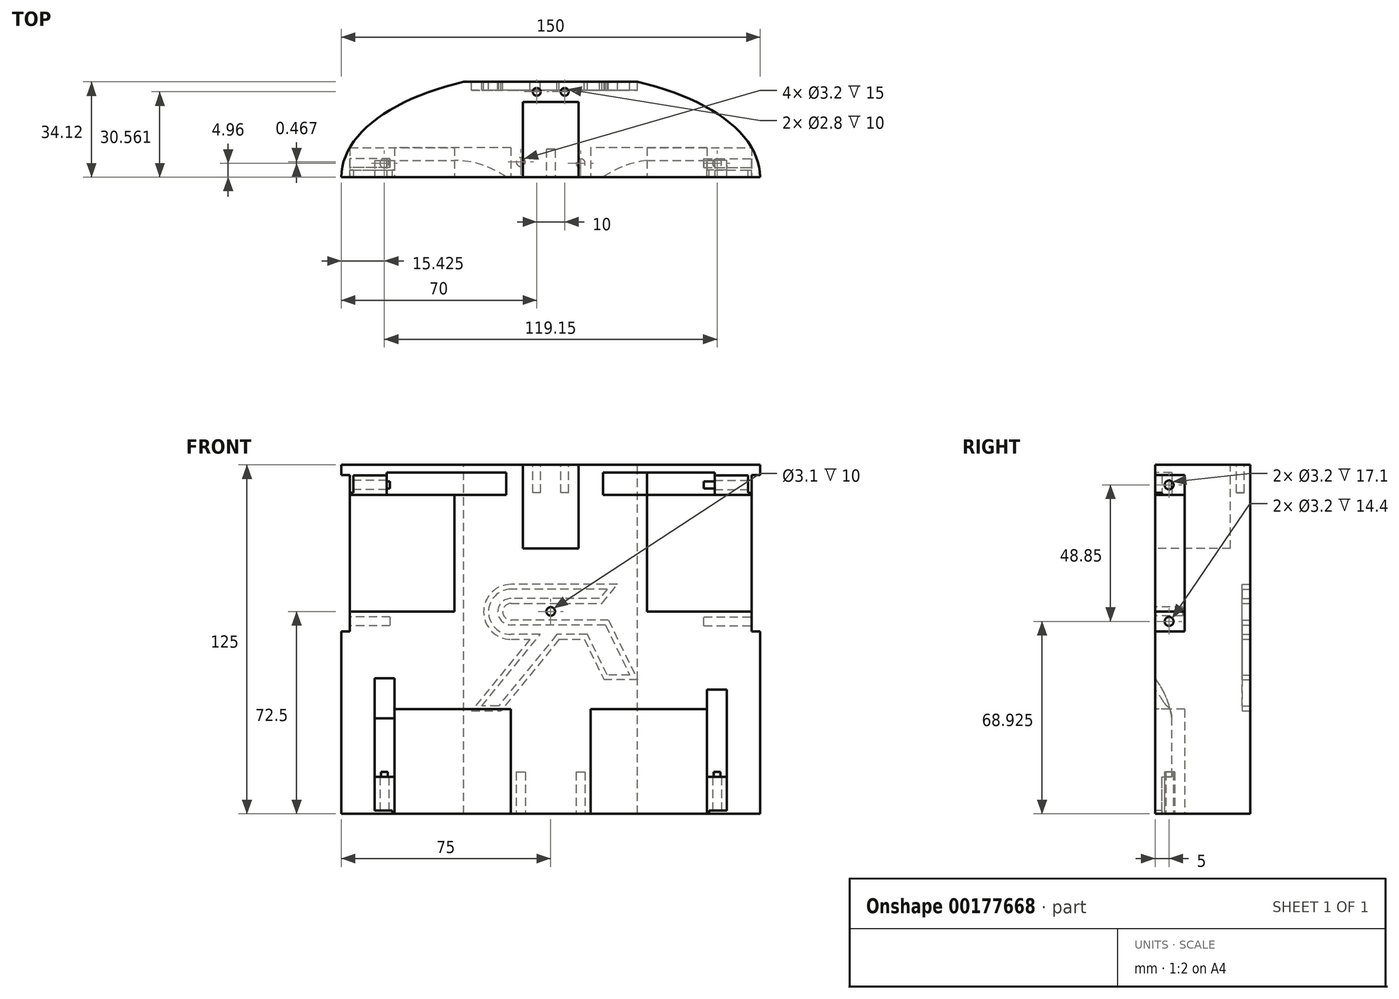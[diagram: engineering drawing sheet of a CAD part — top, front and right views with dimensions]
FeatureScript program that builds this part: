
annotation { "Feature Type Name" : "Feature", "Feature Type Description" : "" }
export const myFeature = defineFeature(function(context is Context, id is Id, definition is map)
    precondition{}
    {
        {
            var Q0;
            Q0=qCreatedBy(makeId("Top.planeOp"),FACE);
            var sketch = newSketch(context, id + "F0", { "sketchPlane" : qUnion([Q0])});
            skLineSegment(sketch, "E0.bottom", {"start": v(-150, 0) * mm, "end": v(0, 0) * mm});
            skLineSegment(sketch, "E0.top", {"start": v(-150, -75) * mm, "end": v(0, -75) * mm});
            skLineSegment(sketch, "E0.left", {"start": v(-150, 0) * mm, "end": v(-150, -75) * mm});
            skLineSegment(sketch, "E0.right", {"start": v(0, 0) * mm, "end": v(0, -75) * mm});
            skLineSegment(sketch, "E1", {"start": v(0, -37.5) * mm, "end": v(-150, -37.5) * mm});
            skPoint(sketch, "E2", {"position": v(-75, -37.5) * mm});
            skEllipse(sketch, "E3", {"center": v(-75, -37.5) * mm, "majorRadius": 75 * mm, "minorRadius": 37.5 * mm, "majorAxis": v(1, 0)});
            skSolve(sketch);
        }
        {
            var Q0;
            {var subQ0=sQuery(id+"F0.wireOp",EDGE,"E1");Q0=makeQuery(id+"F0.imprint","IMPRINT",FACE,{"disambiguationData":[TD([[makeQuery(id+"F0.imprint","IMPRINT",EDGE,{"derivedFrom":subQ0}),1.0]])]});}
            var Q1;
            {var subQ0=sQuery(id+"F0.wireOp",EDGE,"E1");Q1=makeQuery(id+"F0.imprint","IMPRINT",FACE,{"disambiguationData":[TD([[makeQuery(id+"F0.imprint","IMPRINT",EDGE,{"derivedFrom":subQ0}),-1.0]])]});}
            extrude(context, id + "F1", {"entities" : qUnion([Q0, Q1]), "depth" : 125 * mm});
        }
        {
            var Q0;
            Q0=qCreatedBy(makeId("Right.planeOp"),FACE);
            var sketch = newSketch(context, id + "F2", { "sketchPlane" : qUnion([Q0])});
            skLineSegment(sketch, "E4.bottom", {"start": v(-48.1, 114.2) * mm, "end": v(-26.9, 114.2) * mm});
            skLineSegment(sketch, "E4.top", {"start": v(-48.1, 72.5) * mm, "end": v(-26.9, 72.5) * mm});
            skLineSegment(sketch, "E4.left", {"start": v(-48.1, 114.2) * mm, "end": v(-48.1, 72.5) * mm});
            skLineSegment(sketch, "E4.right", {"start": v(-26.9, 114.2) * mm, "end": v(-26.9, 72.5) * mm});
            skPoint(sketch, "E5", {"position": v(-37.5, 125) * mm});
            skPoint(sketch, "E6", {"position": v(-37.5, 114.2) * mm});
            skLineSegment(sketch, "E7", {"start": v(-37.5, 125) * mm, "end": v(-37.5, 121.35) * mm});
            skLineSegment(sketch, "E8.bottom", {"start": v(-48.1, 113.35) * mm, "end": v(-26.9, 113.35) * mm, "construction": true});
            skLineSegment(sketch, "E8.top", {"start": v(-48.1, 73.35) * mm, "end": v(-26.9, 73.35) * mm, "construction": true});
            skLineSegment(sketch, "E8.left", {"start": v(-48.1, 113.35) * mm, "end": v(-48.1, 73.35) * mm, "construction": true});
            skLineSegment(sketch, "E8.right", {"start": v(-26.9, 113.35) * mm, "end": v(-26.9, 73.35) * mm, "construction": true});
            skPoint(sketch, "E9", {"position": v(-26.9, 93.35) * mm});
            skLineSegment(sketch, "E10.bottom", {"start": v(-48.1, 113.35) * mm, "end": v(-26.9, 113.35) * mm});
            skLineSegment(sketch, "E10.top", {"start": v(-48.1, 121.35) * mm, "end": v(-26.9, 121.35) * mm});
            skLineSegment(sketch, "E10.left", {"start": v(-48.1, 113.35) * mm, "end": v(-48.1, 121.35) * mm});
            skLineSegment(sketch, "E10.right", {"start": v(-26.9, 113.35) * mm, "end": v(-26.9, 121.35) * mm});
            skLineSegment(sketch, "E11.bottom", {"start": v(-48.1, 73.35) * mm, "end": v(-26.9, 73.35) * mm});
            skLineSegment(sketch, "E11.top", {"start": v(-48.1, 65.35) * mm, "end": v(-26.9, 65.35) * mm});
            skLineSegment(sketch, "E11.left", {"start": v(-48.1, 73.35) * mm, "end": v(-48.1, 65.35) * mm});
            skLineSegment(sketch, "E11.right", {"start": v(-26.9, 73.35) * mm, "end": v(-26.9, 65.35) * mm});
            skLineSegment(sketch, "E12", {"start": v(-37.5, 65.35) * mm, "end": v(-37.5, 0) * mm});
            skLineSegment(sketch, "E13", {"start": v(-37.5, 121.35) * mm, "end": v(-37.5, 125) * mm});
            skLineSegment(sketch, "E14.trimOffspring", {"start": v(-37.5, 114.2) * mm, "end": v(-37.5, 72.5) * mm});
            skSolve(sketch);
        }
        {
            var Q0;
            {var subQ0=sQuery(id+"F2.wireOp",EDGE,"E4.right");Q0=makeQuery(id+"F2.imprint","IMPRINT",FACE,{"disambiguationData":[TD([[makeQuery(id+"F2.imprint","IMPRINT",EDGE,{"derivedFrom":subQ0}),-1.0]])]});}
            var Q1;
            {var subQ0=sQuery(id+"F2.wireOp",EDGE,"E4.left");Q1=makeQuery(id+"F2.imprint","IMPRINT",FACE,{"disambiguationData":[TD([[makeQuery(id+"F2.imprint","IMPRINT",EDGE,{"derivedFrom":subQ0}),1.0]])]});}
            var Q2;
            {var subQ0=sQuery(id+"F2.wireOp",EDGE,"E11.left");var subQ1=sQuery(id+"F2.wireOp",EDGE,"E4.top");var subQ2=makeQuery(id+"F2.imprint","INTERSECT",VERTEX,{"derivedFrom":[subQ1,subQ0]});Q2=makeQuery(id+"F2.imprint","IMPRINT",FACE,{"disambiguationData":[TD([[makeQuery(id+"F2.imprint","IMPRINT",EDGE,{"disambiguationData":[TD([[subQ2,-1.0]])],"derivedFrom":subQ1}),1.0]])]});}
            var Q3;
            {var subQ0=sQuery(id+"F2.wireOp",EDGE,"E11.right");var subQ1=sQuery(id+"F2.wireOp",EDGE,"E4.top");var subQ2=makeQuery(id+"F2.imprint","INTERSECT",VERTEX,{"derivedFrom":[subQ1,subQ0]});Q3=makeQuery(id+"F2.imprint","IMPRINT",FACE,{"disambiguationData":[TD([[makeQuery(id+"F2.imprint","IMPRINT",EDGE,{"disambiguationData":[TD([[subQ2,1.0]])],"derivedFrom":subQ1}),1.0]])]});}
            var Q4;
            {var subQ0=sQuery(id+"F2.wireOp",EDGE,"E10.left");var subQ1=sQuery(id+"F2.wireOp",EDGE,"E4.bottom");var subQ2=makeQuery(id+"F2.imprint","INTERSECT",VERTEX,{"derivedFrom":[subQ1,subQ0]});Q4=makeQuery(id+"F2.imprint","IMPRINT",FACE,{"disambiguationData":[TD([[makeQuery(id+"F2.imprint","IMPRINT",EDGE,{"disambiguationData":[TD([[subQ2,-1.0]])],"derivedFrom":subQ1}),-1.0]])]});}
            var Q5;
            {var subQ0=sQuery(id+"F2.wireOp",EDGE,"E10.right");var subQ1=sQuery(id+"F2.wireOp",EDGE,"E4.bottom");var subQ2=makeQuery(id+"F2.imprint","INTERSECT",VERTEX,{"derivedFrom":[subQ1,subQ0]});Q5=makeQuery(id+"F2.imprint","IMPRINT",FACE,{"disambiguationData":[TD([[makeQuery(id+"F2.imprint","IMPRINT",EDGE,{"disambiguationData":[TD([[subQ2,1.0]])],"derivedFrom":subQ1}),-1.0]])]});}
            extrude(context, id + "F3", {"entities" : qUnion([Q0, Q1, Q2, Q3, Q4, Q5]), "operationType" : NewBodyOperationType.REMOVE, "oppositeDirection" : true, "depth" : 155.5 * mm});
        }
        {
            var Q0;
            Q0=makeQuery(id+"F3.boolean.opBoolean","COPY",FACE,{"derivedFrom":makeQuery(id+"F3.opExtrude","SWEPT_FACE",FACE,{"disambiguationData":[OSD([sQuery(id+"F2.wireOp",EDGE,"E4.top")])]})});
            var sketch = newSketch(context, id + "F4", { "sketchPlane" : qUnion([Q0])});
            skLineSegment(sketch, "E15", {"start": v(-3.06, -48.1) * mm, "end": v(-3.06, -26.9) * mm});
            skEllipticalArc(sketch, "E16.0", {});
            skLineSegment(sketch, "E17", {"start": v(-146.94, -48.1) * mm, "end": v(-146.94, -26.9) * mm});
            skEllipticalArc(sketch, "E18.0", {});
            const initialGuessF4  = {"E16.0": [-0.075, -0.0375, 1, 0, 0.075, 0.0375, 5.996612290444908, 0.28657301673467844], "E18.0": [-0.075, -0.0375, 1, 0, 0.075, 0.0375, 2.855019636855115, 3.428165670324471]};
            skSetInitialGuess(sketch, initialGuessF4);
            skSolve(sketch);
        }
        {
            var Q0;
            Q0=makeQuery(id+"F4.imprint","IMPRINT",FACE,{"disambiguationData":[TD([[makeQuery(id+"F4.imprint","IMPRINT",EDGE,{"derivedFrom":sQuery(id+"F4.wireOp",EDGE,"E17")}),1.0]])]});
            var Q1;
            Q1=makeQuery(id+"F4.imprint","IMPRINT",FACE,{"disambiguationData":[TD([[makeQuery(id+"F4.imprint","IMPRINT",EDGE,{"derivedFrom":sQuery(id+"F4.wireOp",EDGE,"E15")}),-1.0]])]});
            extrude(context, id + "F5", {"entities" : qUnion([Q0, Q1]), "operationType" : NewBodyOperationType.REMOVE, "oppositeDirection" : true, "depth" : 7.15 * mm});
        }
        {
            var Q0;
            Q0=makeQuery(id+"F3.boolean.opBoolean","COPY",FACE,{"derivedFrom":makeQuery(id+"F3.opExtrude","SWEPT_FACE",FACE,{"disambiguationData":[OSD([sQuery(id+"F2.wireOp",EDGE,"E4.bottom")])]})});
            var sketch = newSketch(context, id + "F6", { "sketchPlane" : qUnion([Q0])});
            skLineSegment(sketch, "E19", {"start": v(-3.06, 26.9) * mm, "end": v(-3.06, 48.1) * mm});
            skEllipticalArc(sketch, "E20.0", {});
            skLineSegment(sketch, "E21", {"start": v(-146.94, 26.9) * mm, "end": v(-146.94, 48.1) * mm});
            skEllipticalArc(sketch, "E22.0", {});
            const initialGuessF6  = {"E20.0": [-0.075, 0.0375, 1, 0, 0.075, 0.0375, 5.996612290444908, 0.28657301673467805], "E22.0": [-0.075, 0.0375, 1, 0, 0.075, 0.0375, 2.8550196368551153, 3.428165670324471]};
            skSetInitialGuess(sketch, initialGuessF6);
            skSolve(sketch);
        }
        {
            var Q0;
            Q0=makeQuery(id+"F6.imprint","IMPRINT",FACE,{"disambiguationData":[TD([[makeQuery(id+"F6.imprint","IMPRINT",EDGE,{"derivedFrom":sQuery(id+"F6.wireOp",EDGE,"E21")}),1.0]])]});
            var Q1;
            Q1=makeQuery(id+"F6.imprint","IMPRINT",FACE,{"disambiguationData":[TD([[makeQuery(id+"F6.imprint","IMPRINT",EDGE,{"derivedFrom":sQuery(id+"F6.wireOp",EDGE,"E19")}),-1.0]])]});
            extrude(context, id + "F7", {"entities" : qUnion([Q0, Q1]), "operationType" : NewBodyOperationType.REMOVE, "oppositeDirection" : true, "depth" : 7.15 * mm});
        }
        {
            var Q0;
            Q0=makeQuery(id+"F3.boolean.opBoolean","COPY",FACE,{"derivedFrom":makeQuery(id+"F3.opExtrude","SWEPT_FACE",FACE,{"disambiguationData":[OSD([sQuery(id+"F2.wireOp",EDGE,"E4.top")])]})});
            var sketch = newSketch(context, id + "F8", { "sketchPlane" : qUnion([Q0])});
            skLineSegment(sketch, "E23.bottom", {"start": v(-109.44, -26.9) * mm, "end": v(-40.56, -26.9) * mm});
            skLineSegment(sketch, "E23.top", {"start": v(-109.44, -48.1) * mm, "end": v(-40.56, -48.1) * mm});
            skLineSegment(sketch, "E23.left", {"start": v(-109.44, -26.9) * mm, "end": v(-109.44, -48.1) * mm});
            skLineSegment(sketch, "E23.right", {"start": v(-40.56, -26.9) * mm, "end": v(-40.56, -48.1) * mm});
            skSolve(sketch);
        }
        {
            var Q0;
            Q0=makeQuery(id+"F8.imprint","IMPRINT",FACE,{"disambiguationData":[TD([[makeQuery(id+"F8.imprint","IMPRINT",EDGE,{"derivedFrom":sQuery(id+"F8.wireOp",EDGE,"E23.bottom")}),-1.0]])]});
            extrude(context, id + "F9", {"entities" : qUnion([Q0]), "operationType" : NewBodyOperationType.ADD, "depth" : 46 * mm});
        }
        {
            var Q0;
            Q0=makeQuery(id+"F9.boolean.opBoolean","SPLIT",FACE,{"disambiguationData":[TD([makeQuery(id+"F7.boolean.opBoolean","COPY",FACE,{"derivedFrom":makeQuery(id+"F7.opExtrude","SWEPT_FACE",FACE,{"disambiguationData":[OSD([sQuery(id+"F6.wireOp",EDGE,"E21")])]})})])],"derivedFrom":makeQuery(id+"F3.boolean.opBoolean","COPY",FACE,{"derivedFrom":makeQuery(id+"F3.opExtrude","SWEPT_FACE",FACE,{"disambiguationData":[OSD([sQuery(id+"F2.wireOp",EDGE,"E4.bottom")])]})})});
            var sketch = newSketch(context, id + "F10", { "sketchPlane" : qUnion([Q0])});
            skLineSegment(sketch, "E24", {"start": v(-145.7, 26.9) * mm, "end": v(-145.7, 48.1) * mm, "construction": true});
            skLineSegment(sketch, "E25", {"start": v(-145.7, 37.5) * mm, "end": v(-142.91, 37.5) * mm});
            skLineSegment(sketch, "E26.bottom", {"start": v(-145.7, 35) * mm, "end": v(-4.3, 35) * mm});
            skLineSegment(sketch, "E26.top", {"start": v(-145.7, 40) * mm, "end": v(-4.3, 40) * mm});
            skLineSegment(sketch, "E26.left", {"start": v(-145.7, 35) * mm, "end": v(-145.7, 40) * mm});
            skLineSegment(sketch, "E26.right", {"start": v(-4.3, 35) * mm, "end": v(-4.3, 40) * mm});
            skLineSegment(sketch, "E27", {"start": v(-4.3, 26.9) * mm, "end": v(-4.3, 48.1) * mm, "construction": true});
            skLineSegment(sketch, "E28", {"start": v(-145.7, 37.5) * mm, "end": v(-145.7, 40) * mm});
            skLineSegment(sketch, "E29", {"start": v(-145.7, 35) * mm, "end": v(-145.7, 37.5) * mm});
            skSolve(sketch);
        }
        {
            var Q0;
            Q0=qSketchRegion(id+"F10",true);
            extrude(context, id + "F11", {"entities" : qUnion([Q0]), "operationType" : NewBodyOperationType.REMOVE, "oppositeDirection" : true, "depth" : 7 * mm});
        }
        {
            var Q0;
            Q0=makeQuery(id+"F9.boolean.opBoolean","SPLIT",FACE,{"disambiguationData":[TD([makeQuery(id+"F7.boolean.opBoolean","COPY",FACE,{"derivedFrom":makeQuery(id+"F7.opExtrude","SWEPT_FACE",FACE,{"disambiguationData":[OSD([sQuery(id+"F6.wireOp",EDGE,"E21")])]})})])],"derivedFrom":makeQuery(id+"F3.boolean.opBoolean","COPY",FACE,{"derivedFrom":makeQuery(id+"F3.opExtrude","SWEPT_FACE",FACE,{"disambiguationData":[OSD([sQuery(id+"F2.wireOp",EDGE,"E4.bottom")])]})})});
            var sketch = newSketch(context, id + "F12", { "sketchPlane" : qUnion([Q0])});
            skLineSegment(sketch, "E30.bottom", {"start": v(-133.7, 31.5) * mm, "end": v(-16.3, 31.5) * mm});
            skLineSegment(sketch, "E30.top", {"start": v(-133.7, 43.5) * mm, "end": v(-16.3, 43.5) * mm});
            skLineSegment(sketch, "E30.left", {"start": v(-133.7, 31.5) * mm, "end": v(-133.7, 43.5) * mm});
            skLineSegment(sketch, "E30.right", {"start": v(-16.3, 31.5) * mm, "end": v(-16.3, 43.5) * mm});
            skLineSegment(sketch, "E31", {"start": v(-133.7, 35) * mm, "end": v(-133.7, 40) * mm});
            skPoint(sketch, "E32", {"position": v(-133.7, 37.5) * mm});
            skLineSegment(sketch, "E33", {"start": v(-16.3, 35) * mm, "end": v(-16.3, 40) * mm});
            skPoint(sketch, "E34", {"position": v(-16.3, 37.5) * mm});
            skSolve(sketch);
        }
        {
            var Q0;
            Q0=qSketchRegion(id+"F12",true);
            extrude(context, id + "F13", {"entities" : qUnion([Q0]), "operationType" : NewBodyOperationType.REMOVE, "oppositeDirection" : true, "depth" : 8 * mm});
        }
        {
            var Q0;
            Q0=makeQuery(id+"F9.boolean.opBoolean","SPLIT",FACE,{"disambiguationData":[TD([makeQuery(id+"F7.boolean.opBoolean","COPY",FACE,{"derivedFrom":makeQuery(id+"F7.opExtrude","SWEPT_FACE",FACE,{"disambiguationData":[OSD([sQuery(id+"F6.wireOp",EDGE,"E21")])]})})])],"derivedFrom":makeQuery(id+"F3.boolean.opBoolean","COPY",FACE,{"derivedFrom":makeQuery(id+"F3.opExtrude","SWEPT_FACE",FACE,{"disambiguationData":[OSD([sQuery(id+"F2.wireOp",EDGE,"E4.bottom")])]})})});
            var sketch = newSketch(context, id + "F14", { "sketchPlane" : qUnion([Q0])});
            skArc(sketch, "E35", {"start": v(-109.44, 31.5) * mm, "mid": v(-83.34, 45.45) * mm, "end": v(-80.45, 74.9) * mm});
            skArc(sketch, "E36", {"start": v(-109.44, 43.5) * mm, "mid": v(-91.99, 53.74) * mm, "end": v(-92.41, 73.98) * mm});
            skEllipticalArc(sketch, "E37.0", {});
            skLineSegment(sketch, "E38", {"start": v(-109.44, 31.5) * mm, "end": v(-109.44, 43.5) * mm});
            skArc(sketch, "E39", {"start": v(-69.55, 74.9) * mm, "mid": v(-65.03, 46.53) * mm, "end": v(-40.56, 31.5) * mm});
            skArc(sketch, "E40", {"start": v(-57.59, 73.98) * mm, "mid": v(-55.43, 55.19) * mm, "end": v(-40.56, 43.5) * mm});
            skEllipticalArc(sketch, "E41.0", {});
            skLineSegment(sketch, "E42", {"start": v(-40.56, 31.5) * mm, "end": v(-40.56, 43.5) * mm});
            skLineSegment(sketch, "E43", {"start": v(-75, 37.5) * mm, "end": v(-75, 74.9) * mm, "construction": true});
            skLineSegment(sketch, "E44", {"start": v(-69.55, 74.9) * mm, "end": v(-75, 74.9) * mm, "construction": true});
            skLineSegment(sketch, "E45", {"start": v(-80.45, 74.9) * mm, "end": v(-75, 74.9) * mm, "construction": true});
            const initialGuessF14  = {"E37.0": [-0.075, 0.0375, 1, 0, 0.075, 0.0375, 1.6434997456011395, 1.8050969396186902], "E41.0": [-0.075, 0.0375, 1, 0, 0.075, 0.0375, 1.3364957139711027, 1.4980929079886538], "E37.0": [-0.075, 0.0375, 1, 0, 0.075, 0.0375, 1.6434997456011395, 1.8050969396186902]};
            skSetInitialGuess(sketch, initialGuessF14);
            skSolve(sketch);
        }
        {
            var Q0;
            Q0=qSketchRegion(id+"F14",true);
            extrude(context, id + "F15", {"entities" : qUnion([Q0]), "operationType" : NewBodyOperationType.REMOVE, "oppositeDirection" : true, "depth" : 8 * mm});
        }
        {
            var Q0;
            Q0=makeQuery(id+"F15.boolean.opBoolean","MERGE",FACE,{"derivedFrom":[makeQuery(id+"F13.boolean.opBoolean","MERGE",FACE,{"derivedFrom":[makeQuery(id+"F11.boolean.opBoolean","COPY",FACE,{"derivedFrom":makeQuery(id+"F11.opExtrude","CAP_FACE",FACE,{"disambiguationData":[OSD([sQuery(id+"F10.wireOp",EDGE,"E26.bottom"),sQuery(id+"F10.wireOp",EDGE,"E26.top"),sQuery(id+"F10.wireOp",EDGE,"E26.right"),sQuery(id+"F10.wireOp",EDGE,"E28"),sQuery(id+"F10.wireOp",EDGE,"E29")])],"isStart":true})}),makeQuery(id+"F13.opExtrude","CAP_FACE",FACE,{"disambiguationData":[OSD([sQuery(id+"F12.wireOp",EDGE,"E30.bottom"),sQuery(id+"F12.wireOp",EDGE,"E30.top"),sQuery(id+"F12.wireOp",EDGE,"E30.left"),sQuery(id+"F12.wireOp",EDGE,"E30.right"),sQuery(id+"F12.wireOp",EDGE,"E31"),sQuery(id+"F12.wireOp",EDGE,"E33")])],"isStart":true})]}),makeQuery(id+"F15.opExtrude","CAP_FACE",FACE,{"disambiguationData":[OSD([sQuery(id+"F14.wireOp",EDGE,"E35"),sQuery(id+"F14.wireOp",EDGE,"E36"),sQuery(id+"F14.wireOp",EDGE,"E38"),sQuery(id+"F14.wireOp",EDGE,"E37.0")])],"isStart":true}),makeQuery(id+"F15.opExtrude","CAP_FACE",FACE,{"disambiguationData":[OSD([sQuery(id+"F14.wireOp",EDGE,"E39"),sQuery(id+"F14.wireOp",EDGE,"E40"),sQuery(id+"F14.wireOp",EDGE,"E41.0"),sQuery(id+"F14.wireOp",EDGE,"E42")])],"isStart":true})]});
            var sketch = newSketch(context, id + "F16", { "sketchPlane" : qUnion([Q0])});
            skArc(sketch, "E46.0", {"start": v(-84.76, -43.5) * mm, "mid": v(-78.35, -58.62) * mm, "end": v(-80.45, -74.9) * mm, "construction": true});
            skArc(sketch, "E46.1", {"start": v(-69.55, -74.9) * mm, "mid": v(-70.05, -58.36) * mm, "end": v(-62.76, -43.5) * mm, "construction": true});
            skLineSegment(sketch, "E47", {"start": v(-62.76, -43.5) * mm, "end": v(-84.76, -43.5) * mm});
            skArc(sketch, "E48", {"start": v(-84.76, -43.5) * mm, "mid": v(-95.72, -34.66) * mm, "end": v(-109.44, -31.5) * mm});
            skArc(sketch, "E49", {"start": v(-40.56, -31.5) * mm, "mid": v(-52.8, -35.39) * mm, "end": v(-62.76, -43.5) * mm});
            skLineSegment(sketch, "E50", {"start": v(-109.44, -31.5) * mm, "end": v(-40.56, -31.5) * mm});
            skSolve(sketch);
        }
        {
            var Q0;
            Q0=qSketchRegion(id+"F16",true);
            extrude(context, id + "F17", {"entities" : qUnion([Q0]), "operationType" : NewBodyOperationType.ADD, "depth" : 9.4 * mm});
        }
        {
            var Q0;
            Q0=makeQuery(id+"F7.boolean.opBoolean","COPY",FACE,{"derivedFrom":makeQuery(id+"F7.opExtrude","SWEPT_FACE",FACE,{"disambiguationData":[OSD([sQuery(id+"F6.wireOp",EDGE,"E19")])]})});
            var sketch = newSketch(context, id + "F18", { "sketchPlane" : qUnion([Q0])});
            skLineSegment(sketch, "E51", {"start": v(-48.1, 117.77) * mm, "end": v(-26.9, 117.77) * mm, "construction": true});
            skCircle(sketch, "E52", {"center": v(-42.5, 117.78) * mm, "radius": 1.6 * mm});
            skCircle(sketch, "E53", {"center": v(-32.5, 117.78) * mm, "radius": 1.6 * mm});
            skLineSegment(sketch, "E54", {"start": v(-32.5, 117.77) * mm, "end": v(-42.5, 117.77) * mm});
            skPoint(sketch, "E55", {"position": v(-37.5, 117.77) * mm});
            skLineSegment(sketch, "E56", {"start": v(-26.9, 68.92) * mm, "end": v(-48.1, 68.92) * mm, "construction": true});
            skCircle(sketch, "E57", {"center": v(-32.5, 68.92) * mm, "radius": 1.6 * mm});
            skCircle(sketch, "E58", {"center": v(-42.5, 68.92) * mm, "radius": 1.6 * mm});
            skPoint(sketch, "E59", {"position": v(-37.5, 68.92) * mm});
            skLineSegment(sketch, "E60", {"start": v(-32.5, 68.92) * mm, "end": v(-42.5, 68.92) * mm});
            skSolve(sketch);
        }
        {
            var Q0;
            Q0=qSketchRegion(id+"F18",true);
            extrude(context, id + "F19", {"entities" : qUnion([Q0]), "operationType" : NewBodyOperationType.REMOVE, "oppositeDirection" : true, "depth" : 17.1 * mm});
        }
        {
            var Q0;
            Q0=makeQuery(id+"F7.boolean.opBoolean","COPY",FACE,{"derivedFrom":makeQuery(id+"F7.opExtrude","SWEPT_FACE",FACE,{"disambiguationData":[OSD([sQuery(id+"F6.wireOp",EDGE,"E21")])]})});
            var sketch = newSketch(context, id + "F20", { "sketchPlane" : qUnion([Q0])});
            skCircle(sketch, "E61.0", {"center": v(32.5, 68.92) * mm, "radius": 1.6 * mm});
            skCircle(sketch, "E61.1", {"center": v(42.5, 68.92) * mm, "radius": 1.6 * mm});
            skCircle(sketch, "E61.2", {"center": v(42.5, 117.78) * mm, "radius": 1.6 * mm});
            skCircle(sketch, "E61.3", {"center": v(32.5, 117.78) * mm, "radius": 1.6 * mm});
            skSolve(sketch);
        }
        {
            var Q0;
            Q0=qSketchRegion(id+"F20",true);
            extrude(context, id + "F21", {"entities" : qUnion([Q0]), "operationType" : NewBodyOperationType.REMOVE, "oppositeDirection" : true, "depth" : 14.4 * mm});
        }
        {
            var Q0;
            Q0=makeQuery(id+"F1.opExtrude","CAP_FACE",FACE,{"disambiguationData":[OSD([sQuery(id+"F0.wireOp",EDGE,"E3")])],"isStart":true});
            var sketch = newSketch(context, id + "F22", { "sketchPlane" : qUnion([Q0])});
            skLineSegment(sketch, "E62", {"start": v(-75, 0) * mm, "end": v(-75, 75) * mm, "construction": true});
            skLineSegment(sketch, "E63.bottom", {"start": v(-19, 26.9) * mm, "end": v(-60.7, 26.9) * mm});
            skLineSegment(sketch, "E63.top", {"start": v(-19, 48.1) * mm, "end": v(-60.7, 48.1) * mm});
            skLineSegment(sketch, "E63.left", {"start": v(-19, 26.9) * mm, "end": v(-19, 48.1) * mm});
            skLineSegment(sketch, "E63.right", {"start": v(-60.7, 26.9) * mm, "end": v(-60.7, 48.1) * mm});
            skLineSegment(sketch, "E64.bottom", {"start": v(-89.3, 26.9) * mm, "end": v(-131, 26.9) * mm});
            skLineSegment(sketch, "E64.top", {"start": v(-89.3, 48.1) * mm, "end": v(-131, 48.1) * mm});
            skLineSegment(sketch, "E64.left", {"start": v(-89.3, 26.9) * mm, "end": v(-89.3, 48.1) * mm});
            skLineSegment(sketch, "E64.right", {"start": v(-131, 26.9) * mm, "end": v(-131, 48.1) * mm});
            skLineSegment(sketch, "E65", {"start": v(-89.3, 37.5) * mm, "end": v(-75, 37.5) * mm});
            skLineSegment(sketch, "E66", {"start": v(-75, 37.5) * mm, "end": v(-60.7, 37.5) * mm});
            skLineSegment(sketch, "E67", {"start": v(-60.7, 37.5) * mm, "end": v(-75, 37.5) * mm, "construction": true});
            skLineSegment(sketch, "E68", {"start": v(-89.3, 37.5) * mm, "end": v(-75, 37.5) * mm, "construction": true});
            skLineSegment(sketch, "E69.bottom", {"start": v(-19.85, 26.9) * mm, "end": v(-59.85, 26.9) * mm});
            skLineSegment(sketch, "E69.top", {"start": v(-19.85, 48.1) * mm, "end": v(-59.85, 48.1) * mm});
            skPoint(sketch, "E70", {"position": v(-39.85, 26.9) * mm});
            skLineSegment(sketch, "E71.bottom", {"start": v(-19.85, 26.9) * mm, "end": v(-11.85, 26.9) * mm});
            skLineSegment(sketch, "E71.top", {"start": v(-19.85, 48.1) * mm, "end": v(-11.85, 48.1) * mm});
            skLineSegment(sketch, "E71.right", {"start": v(-11.85, 26.9) * mm, "end": v(-11.85, 48.1) * mm});
            skLineSegment(sketch, "E72.bottom", {"start": v(-60.7, 48.1) * mm, "end": v(-67.85, 48.1) * mm});
            skLineSegment(sketch, "E72.top", {"start": v(-60.7, 26.9) * mm, "end": v(-67.85, 26.9) * mm});
            skLineSegment(sketch, "E72.left", {"start": v(-60.7, 48.1) * mm, "end": v(-60.7, 26.9) * mm});
            skLineSegment(sketch, "E72.right", {"start": v(-67.85, 48.1) * mm, "end": v(-67.85, 26.9) * mm});
            skPoint(sketch, "E73.oppositeSnap0", {"position": v(-82.15, 37.5) * mm});
            skLineSegment(sketch, "E73.bottom", {"start": v(-89.3, 26.9) * mm, "end": v(-82.15, 26.9) * mm});
            skLineSegment(sketch, "E73.top", {"start": v(-89.3, 48.1) * mm, "end": v(-82.15, 48.1) * mm});
            skLineSegment(sketch, "E73.right", {"start": v(-82.15, 26.9) * mm, "end": v(-82.15, 48.1) * mm});
            skLineSegment(sketch, "E74.bottom", {"start": v(-131, 26.9) * mm, "end": v(-138.15, 26.9) * mm});
            skLineSegment(sketch, "E74.top", {"start": v(-131, 48.1) * mm, "end": v(-138.15, 48.1) * mm});
            skLineSegment(sketch, "E74.right", {"start": v(-138.15, 26.9) * mm, "end": v(-138.15, 48.1) * mm});
            skLineSegment(sketch, "E75.bottom", {"start": v(-90.15, 26.9) * mm, "end": v(-130.15, 26.9) * mm});
            skLineSegment(sketch, "E75.top", {"start": v(-90.15, 48.1) * mm, "end": v(-130.15, 48.1) * mm});
            skPoint(sketch, "E76", {"position": v(-110.15, 26.9) * mm});
            skPoint(sketch, "E77", {"position": v(-67.85, 37.5) * mm});
            skLineSegment(sketch, "E78", {"start": v(-19, 26.9) * mm, "end": v(-11.85, 26.9) * mm});
            skLineSegment(sketch, "E79", {"start": v(-19, 48.1) * mm, "end": v(-11.85, 48.1) * mm});
            skCircle(sketch, "E80", {"center": v(-15.42, 32.53) * mm, "radius": 1.6 * mm});
            skCircle(sketch, "E81", {"center": v(-15.42, 42.53) * mm, "radius": 1.6 * mm});
            skCircle(sketch, "E82", {"center": v(-64.27, 32.54) * mm, "radius": 1.6 * mm});
            skCircle(sketch, "E83", {"center": v(-64.27, 42.54) * mm, "radius": 1.6 * mm});
            skCircle(sketch, "E84", {"center": v(-85.73, 42.07) * mm, "radius": 1.6 * mm});
            skCircle(sketch, "E85", {"center": v(-85.73, 32.07) * mm, "radius": 1.6 * mm});
            skCircle(sketch, "E86", {"center": v(-134.57, 32.51) * mm, "radius": 1.6 * mm});
            skCircle(sketch, "E87", {"center": v(-134.57, 42.51) * mm, "radius": 1.6 * mm});
            skLineSegment(sketch, "E88", {"start": v(-138.15, 37.5) * mm, "end": v(-11.85, 37.5) * mm, "construction": true});
            skLineSegment(sketch, "E89", {"start": v(-15.42, 32.53) * mm, "end": v(-15.42, 42.53) * mm});
            skLineSegment(sketch, "E90", {"start": v(-64.27, 32.54) * mm, "end": v(-64.27, 42.54) * mm});
            skLineSegment(sketch, "E91", {"start": v(-85.73, 32.07) * mm, "end": v(-85.73, 42.07) * mm});
            skLineSegment(sketch, "E92", {"start": v(-134.57, 32.51) * mm, "end": v(-134.57, 42.51) * mm});
            skSolve(sketch);
        }
        {
            var Q0;
            {var subQ0=sQuery(id+"F22.wireOp",EDGE,"E63.left");Q0=makeQuery(id+"F22.imprint","IMPRINT",FACE,{"disambiguationData":[TD([[makeQuery(id+"F22.imprint","IMPRINT",EDGE,{"derivedFrom":subQ0}),1.0]])]});}
            var Q1;
            {var subQ1=sQuery(id+"F22.wireOp",EDGE,"E63.bottom");Q1=makeQuery(id+"F22.imprint","IMPRINT",FACE,{"disambiguationData":[TD([[makeQuery(id+"F22.imprint","IMPRINT",EDGE,{"derivedFrom":subQ1}),-1.0]])]});}
            var Q2;
            {var subQ0=sQuery(id+"F22.wireOp",EDGE,"E64.right");Q2=makeQuery(id+"F22.imprint","IMPRINT",FACE,{"disambiguationData":[TD([[makeQuery(id+"F22.imprint","IMPRINT",EDGE,{"derivedFrom":subQ0}),-1.0]])]});}
            extrude(context, id + "F23", {"entities" : qUnion([Q0, Q1, Q2]), "operationType" : NewBodyOperationType.REMOVE, "oppositeDirection" : true, "depth" : 37.5 * mm});
        }
        {
            var Q0;
            Q0=makeQuery(id+"F22.imprint","IMPRINT",FACE,{"disambiguationData":[TD([[makeQuery(id+"F22.imprint","IMPRINT",EDGE,{"derivedFrom":sQuery(id+"F22.wireOp",EDGE,"E80")}),1.0]])]});
            var Q1;
            Q1=makeQuery(id+"F22.imprint","IMPRINT",FACE,{"disambiguationData":[TD([[makeQuery(id+"F22.imprint","IMPRINT",EDGE,{"derivedFrom":sQuery(id+"F22.wireOp",EDGE,"E81")}),1.0]])]});
            var Q2;
            Q2=makeQuery(id+"F22.imprint","IMPRINT",FACE,{"disambiguationData":[TD([[makeQuery(id+"F22.imprint","IMPRINT",EDGE,{"derivedFrom":sQuery(id+"F22.wireOp",EDGE,"E82")}),1.0]])]});
            var Q3;
            Q3=makeQuery(id+"F22.imprint","IMPRINT",FACE,{"disambiguationData":[TD([[makeQuery(id+"F22.imprint","IMPRINT",EDGE,{"derivedFrom":sQuery(id+"F22.wireOp",EDGE,"E83")}),1.0]])]});
            var Q4;
            Q4=makeQuery(id+"F22.imprint","IMPRINT",FACE,{"disambiguationData":[TD([[makeQuery(id+"F22.imprint","IMPRINT",EDGE,{"derivedFrom":sQuery(id+"F22.wireOp",EDGE,"E85")}),1.0]])]});
            var Q5;
            Q5=makeQuery(id+"F22.imprint","IMPRINT",FACE,{"disambiguationData":[TD([[makeQuery(id+"F22.imprint","IMPRINT",EDGE,{"derivedFrom":sQuery(id+"F22.wireOp",EDGE,"E84")}),1.0]])]});
            var Q6;
            Q6=makeQuery(id+"F22.imprint","IMPRINT",FACE,{"disambiguationData":[TD([[makeQuery(id+"F22.imprint","IMPRINT",EDGE,{"derivedFrom":sQuery(id+"F22.wireOp",EDGE,"E86")}),1.0]])]});
            var Q7;
            Q7=makeQuery(id+"F22.imprint","IMPRINT",FACE,{"disambiguationData":[TD([[makeQuery(id+"F22.imprint","IMPRINT",EDGE,{"derivedFrom":sQuery(id+"F22.wireOp",EDGE,"E87")}),1.0]])]});
            extrude(context, id + "F24", {"entities" : qUnion([Q0, Q1, Q2, Q3, Q4, Q5, Q6, Q7]), "operationType" : NewBodyOperationType.REMOVE, "oppositeDirection" : true, "depth" : 15 * mm});
        }
        {
            var Q0;
            Q0=makeQuery(id+"F23.boolean.opBoolean","COPY",FACE,{"derivedFrom":makeQuery(id+"F23.opExtrude","SWEPT_FACE",FACE,{"disambiguationData":[OSD([sQuery(id+"F22.wireOp",EDGE,"E64.right")])]})});
            var sketch = newSketch(context, id + "F25", { "sketchPlane" : qUnion([Q0])});
            skLineSegment(sketch, "E93.bottom", {"start": v(-35, 1.25) * mm, "end": v(-40, 1.25) * mm});
            skLineSegment(sketch, "E93.left", {"start": v(-35, 1.25) * mm, "end": v(-35, 13.25) * mm});
            skLineSegment(sketch, "E93.right", {"start": v(-40, 1.25) * mm, "end": v(-40, 13.25) * mm});
            skLineSegment(sketch, "E94", {"start": v(-37.5, 0) * mm, "end": v(-37.5, 13.25) * mm, "construction": true});
            skLineSegment(sketch, "E95", {"start": v(-37.5, 1.25) * mm, "end": v(-35, 1.25) * mm});
            skPoint(sketch, "E95.startSnap0", {"position": v(-37.5, 1.25) * mm});
            skLineSegment(sketch, "E96", {"start": v(-37.5, 1.25) * mm, "end": v(-40, 1.25) * mm});
            skPoint(sketch, "E97", {"position": v(-37.5, 31.05) * mm});
            skLineSegment(sketch, "E98.bottom", {"start": v(-31.5, 13.25) * mm, "end": v(-35, 13.25) * mm});
            skLineSegment(sketch, "E98.left", {"start": v(-31.5, 13.25) * mm, "end": v(-31.5, 34.22) * mm});
            skLineSegment(sketch, "E98.right", {"start": v(-43.5, 13.25) * mm, "end": v(-43.5, 34.22) * mm});
            skPoint(sketch, "E99.trimOffspring.end.orphan", {"position": v(-37.5, 32.45) * mm});
            skPoint(sketch, "E100.start.orphan", {"position": v(-40, 31.05) * mm});
            skPoint(sketch, "E93.top.start.orphan", {"position": v(-35, 31.05) * mm});
            skLineSegment(sketch, "E101.trimOffspring", {"start": v(-40, 13.25) * mm, "end": v(-43.5, 13.25) * mm});
            skLineSegment(sketch, "E102", {"start": v(-40, 13.25) * mm, "end": v(-35, 13.25) * mm});
            skLineSegment(sketch, "E103", {"start": v(-43.5, 13.25) * mm, "end": v(-31.5, 13.25) * mm});
            skLineSegment(sketch, "E104", {"start": v(-37.5, 34.22) * mm, "end": v(-37.5, 13.25) * mm});
            skArc(sketch, "E105", {"start": v(-43.5, 34.22) * mm, "mid": v(-54.18, 46.6) * mm, "end": v(-70.51, 47.22) * mm});
            skArc(sketch, "E106", {"start": v(-31.5, 34.22) * mm, "mid": v(-45.26, 55.7) * mm, "end": v(-70.51, 59.22) * mm});
            skLineSegment(sketch, "E107", {"start": v(-43.5, 34.22) * mm, "end": v(-31.5, 34.22) * mm});
            skLineSegment(sketch, "E108", {"start": v(-70.51, 59.22) * mm, "end": v(-70.51, 47.22) * mm});
            skPoint(sketch, "E109.orphan", {"position": v(-31.5, 37.5) * mm});
            skPoint(sketch, "E110.orphan", {"position": v(-37.5, 37.5) * mm});
            skPoint(sketch, "E98.top.end.orphan", {"position": v(-43.5, 37.5) * mm});
            skSolve(sketch);
        }
        {
            var Q0;
            Q0=qSketchRegion(id+"F25",true);
            extrude(context, id + "F26", {"entities" : qUnion([Q0]), "operationType" : NewBodyOperationType.REMOVE, "oppositeDirection" : true, "depth" : 7 * mm});
        }
        {
            var Q0;
            Q0=makeQuery(id+"F23.boolean.opBoolean","COPY",FACE,{"derivedFrom":makeQuery(id+"F23.opExtrude","SWEPT_FACE",FACE,{"disambiguationData":[OSD([sQuery(id+"F22.wireOp",EDGE,"E63.left")])]})});
            var sketch = newSketch(context, id + "F27", { "sketchPlane" : qUnion([Q0])});
            skLineSegment(sketch, "E111.0.2", {"start": v(43.5, 34.22) * mm, "end": v(43.5, 13.25) * mm});
            skLineSegment(sketch, "E111.0.3", {"start": v(43.5, 13.25) * mm, "end": v(40, 13.25) * mm});
            skLineSegment(sketch, "E111.0.4", {"start": v(40, 13.25) * mm, "end": v(40, 1.25) * mm});
            skLineSegment(sketch, "E111.0.5", {"start": v(40, 1.25) * mm, "end": v(35, 1.25) * mm});
            skLineSegment(sketch, "E111.0.6", {"start": v(35, 1.25) * mm, "end": v(35, 13.25) * mm});
            skLineSegment(sketch, "E111.0.7", {"start": v(35, 13.25) * mm, "end": v(31.5, 13.25) * mm});
            skLineSegment(sketch, "E111.0.8", {"start": v(31.5, 13.25) * mm, "end": v(31.5, 34.22) * mm});
            skLineSegment(sketch, "E112", {"start": v(57.85, 60.27) * mm, "end": v(57.85, 47.95) * mm});
            skArc(sketch, "E113", {"start": v(57.85, 60.27) * mm, "mid": v(39.24, 52.75) * mm, "end": v(31.5, 34.22) * mm});
            skArc(sketch, "E114", {"start": v(57.85, 47.95) * mm, "mid": v(47.74, 44.15) * mm, "end": v(43.5, 34.22) * mm});
            skSolve(sketch);
        }
        {
            var Q0;
            {var subQ0=sQuery(id+"F27.wireOp",EDGE,"E111.0.2");Q0=makeQuery(id+"F27.imprint","IMPRINT",FACE,{"disambiguationData":[TD([[makeQuery(id+"F27.imprint","IMPRINT",EDGE,{"derivedFrom":subQ0}),-1.0]])]});}
            extrude(context, id + "F28", {"entities" : qUnion([Q0]), "operationType" : NewBodyOperationType.REMOVE, "oppositeDirection" : true, "depth" : 7 * mm});
        }
        {
            var Q0;
            Q0=makeQuery(id+"F23.boolean.opBoolean","COPY",FACE,{"derivedFrom":makeQuery(id+"F23.opExtrude","SWEPT_FACE",FACE,{"disambiguationData":[OSD([sQuery(id+"F22.wireOp",EDGE,"E63.left")])]})});
            var sketch = newSketch(context, id + "F29", { "sketchPlane" : qUnion([Q0])});
            skArc(sketch, "E115", {"start": v(80.51, 59.28) * mm, "mid": v(51.36, 55.84) * mm, "end": v(31.5, 34.22) * mm});
            skArc(sketch, "E116", {"start": v(82.64, 47.28) * mm, "mid": v(60.63, 48.07) * mm, "end": v(43.5, 34.22) * mm});
            skLineSegment(sketch, "E117", {"start": v(80.51, 59.28) * mm, "end": v(82.64, 47.28) * mm});
            skPoint(sketch, "E118.0", {"position": v(31.5, 34.22) * mm});
            skPoint(sketch, "E118.1", {"position": v(43.5, 34.22) * mm});
            skLineSegment(sketch, "E119", {"start": v(31.5, 34.22) * mm, "end": v(43.5, 34.22) * mm});
            skSolve(sketch);
        }
        {
            var Q0;
            Q0=qSketchRegion(id+"F29",true);
            extrude(context, id + "F30", {"entities" : qUnion([Q0]), "operationType" : NewBodyOperationType.REMOVE, "oppositeDirection" : true, "depth" : 7 * mm});
        }
        {
            var Q0;
            Q0=qCreatedBy(makeId("Right.planeOp"),FACE);
            var sketch = newSketch(context, id + "F31", { "sketchPlane" : qUnion([Q0])});
            skLineSegment(sketch, "E120.bottom", {"start": v(-37.5, 159.6) * mm, "end": v(-92.54, 159.6) * mm});
            skLineSegment(sketch, "E120.top", {"start": v(-37.5, -19.85) * mm, "end": v(-92.54, -19.85) * mm});
            skLineSegment(sketch, "E120.left", {"start": v(-37.5, 159.6) * mm, "end": v(-37.5, -19.85) * mm});
            skLineSegment(sketch, "E120.right", {"start": v(-92.54, 159.6) * mm, "end": v(-92.54, -19.85) * mm});
            skSolve(sketch);
        }
        {
            var Q0;
            Q0=qSketchRegion(id+"F31",true);
            extrude(context, id + "F32", {"entities" : qUnion([Q0]), "operationType" : NewBodyOperationType.REMOVE, "oppositeDirection" : true, "depth" : 197 * mm});
        }
        {
            var Q0;
            Q0=makeQuery(id+"F32.boolean.opBoolean","COPY",FACE,{"derivedFrom":makeQuery(id+"F32.opExtrude","SWEPT_FACE",FACE,{"disambiguationData":[OSD([sQuery(id+"F31.wireOp",EDGE,"E120.left")])]})});
            var sketch = newSketch(context, id + "F33", { "sketchPlane" : qUnion([Q0])});
            skLineSegment(sketch, "E121", {"start": v(-40.56, 72.5) * mm, "end": v(-109.44, 72.5) * mm});
            skCircle(sketch, "E122", {"center": v(-75, 72.5) * mm, "radius": 1.55 * mm});
            skLineSegment(sketch, "E123", {"start": v(-75, 123.57) * mm, "end": v(-75, -4.49) * mm, "construction": true});
            skSolve(sketch);
        }
        {
            var Q0;
            Q0=qSketchRegion(id+"F33",true);
            extrude(context, id + "F34", {"entities" : qUnion([Q0]), "operationType" : NewBodyOperationType.REMOVE, "oppositeDirection" : true, "depth" : 10 * mm});
        }
        {
            var Q0;
            {var subQ0=sQuery(id+"F22.wireOp",EDGE,"E63.left");Q0=makeQuery(id+"F30.boolean.opBoolean","INTERSECT",EDGE,{"derivedFrom":[makeQuery(id+"F28.boolean.opBoolean","MERGE",FACE,{"derivedFrom":[makeQuery(id+"F23.boolean.opBoolean","COPY",FACE,{"derivedFrom":makeQuery(id+"F23.opExtrude","CAP_FACE",FACE,{"disambiguationData":[OSD([sQuery(id+"F22.wireOp",EDGE,"E63.bottom"),sQuery(id+"F22.wireOp",EDGE,"E63.top"),subQ0,sQuery(id+"F22.wireOp",EDGE,"E69.bottom"),sQuery(id+"F22.wireOp",EDGE,"E69.top"),sQuery(id+"F22.wireOp",EDGE,"E71.bottom"),sQuery(id+"F22.wireOp",EDGE,"E71.top"),sQuery(id+"F22.wireOp",EDGE,"E72.left")])],"isStart":false})}),makeQuery(id+"F28.opExtrude","SWEPT_FACE",FACE,{"disambiguationData":[OSD([subQ0])]})]}),makeQuery(id+"F30.opExtrude","SWEPT_FACE",FACE,{"disambiguationData":[OSD([sQuery(id+"F29.wireOp",EDGE,"E115")])]})]});}
            fillet(context, id + "F35", {"entities" : qUnion([Q0]), "radius" : 5 * mm, "tangentPropagation" : true, "allowEdgeOverflow" : false});
        }
        {
            var Q0;
            {var subQ0=sQuery(id+"F22.wireOp",EDGE,"E63.left");Q0=makeQuery(id+"F35.opFillet","BLEND_EDGE",EDGE,{"blendedFrom":[makeQuery(id+"F30.boolean.opBoolean","INTERSECT",EDGE,{"derivedFrom":[makeQuery(id+"F28.boolean.opBoolean","MERGE",FACE,{"derivedFrom":[makeQuery(id+"F23.boolean.opBoolean","COPY",FACE,{"derivedFrom":makeQuery(id+"F23.opExtrude","CAP_FACE",FACE,{"disambiguationData":[OSD([sQuery(id+"F22.wireOp",EDGE,"E63.bottom"),sQuery(id+"F22.wireOp",EDGE,"E63.top"),subQ0,sQuery(id+"F22.wireOp",EDGE,"E69.bottom"),sQuery(id+"F22.wireOp",EDGE,"E69.top"),sQuery(id+"F22.wireOp",EDGE,"E71.bottom"),sQuery(id+"F22.wireOp",EDGE,"E71.top"),sQuery(id+"F22.wireOp",EDGE,"E72.left")])],"isStart":false})}),makeQuery(id+"F28.opExtrude","SWEPT_FACE",FACE,{"disambiguationData":[OSD([subQ0])]})]}),makeQuery(id+"F30.opExtrude","SWEPT_FACE",FACE,{"disambiguationData":[OSD([sQuery(id+"F29.wireOp",EDGE,"E115")])]})]}),makeQuery(id+"F28.boolean.opBoolean","COPY",FACE,{"derivedFrom":makeQuery(id+"F28.opExtrude","SWEPT_FACE",FACE,{"disambiguationData":[OSD([sQuery(id+"F27.wireOp",EDGE,"E113")])]})})],"blendedInto":[makeQuery(id+"F28.boolean.opBoolean","COPY",FACE,{"derivedFrom":makeQuery(id+"F28.opExtrude","SWEPT_FACE",FACE,{"disambiguationData":[OSD([sQuery(id+"F27.wireOp",EDGE,"E113")])]})})]});}
            fillet(context, id + "F49", {"entities" : qUnion([Q0]), "radius" : 5 * mm, "tangentPropagation" : true, "allowEdgeOverflow" : false});
        }
        {
            var Q0;
            Q0=makeQuery(id+"F7.boolean.opBoolean","COPY",FACE,{"derivedFrom":makeQuery(id+"F7.opExtrude","SWEPT_FACE",FACE,{"disambiguationData":[OSD([sQuery(id+"F6.wireOp",EDGE,"E19")])]})});
            var sketch = newSketch(context, id + "F36", { "sketchPlane" : qUnion([Q0])});
            skLineSegment(sketch, "E124.bottom", {"start": v(-37.5, 114.2) * mm, "end": v(-35, 114.2) * mm});
            skLineSegment(sketch, "E124.top", {"start": v(-37.5, 114.95) * mm, "end": v(-35, 114.95) * mm});
            skLineSegment(sketch, "E124.left", {"start": v(-37.5, 114.2) * mm, "end": v(-37.5, 114.95) * mm});
            skLineSegment(sketch, "E124.right", {"start": v(-35, 114.2) * mm, "end": v(-35, 114.95) * mm});
            skSolve(sketch);
        }
        {
            var Q0;
            Q0=qSketchRegion(id+"F36",true);
            extrude(context, id + "F37", {"entities" : qUnion([Q0]), "operationType" : NewBodyOperationType.REMOVE, "oppositeDirection" : true, "depth" : 25 * mm});
        }
        {
            var Q0;
            Q0=makeQuery(id+"F7.boolean.opBoolean","COPY",FACE,{"derivedFrom":makeQuery(id+"F7.opExtrude","SWEPT_FACE",FACE,{"disambiguationData":[OSD([sQuery(id+"F6.wireOp",EDGE,"E21")])]})});
            var sketch = newSketch(context, id + "F38", { "sketchPlane" : qUnion([Q0])});
            skLineSegment(sketch, "E125.bottom", {"start": v(37.5, 114.2) * mm, "end": v(35, 114.2) * mm});
            skLineSegment(sketch, "E125.top", {"start": v(37.5, 114.95) * mm, "end": v(35, 114.95) * mm});
            skLineSegment(sketch, "E125.left", {"start": v(37.5, 114.2) * mm, "end": v(37.5, 114.95) * mm});
            skLineSegment(sketch, "E125.right", {"start": v(35, 114.2) * mm, "end": v(35, 114.95) * mm});
            skSolve(sketch);
        }
        {
            var Q0;
            Q0=qSketchRegion(id+"F38",true);
            extrude(context, id + "F39", {"entities" : qUnion([Q0]), "operationType" : NewBodyOperationType.REMOVE, "oppositeDirection" : true, "depth" : 25 * mm});
        }
        {
            var Q0;
            Q0=makeQuery(id+"F1.opExtrude","CAP_FACE",FACE,{"disambiguationData":[OSD([sQuery(id+"F0.wireOp",EDGE,"E3")])],"isStart":false});
            var sketch = newSketch(context, id + "F40", { "sketchPlane" : qUnion([Q0])});
            skLineSegment(sketch, "E126", {"start": v(-75, -3.38) * mm, "end": v(-75, -37.5) * mm});
            skLineSegment(sketch, "E127", {"start": v(-106.11, -3.38) * mm, "end": v(-43.89, -3.38) * mm});
            skEllipticalArc(sketch, "E128.0", {});
            skPoint(sketch, "E129.orphan", {"position": v(-150, -37.5) * mm});
            skPoint(sketch, "E130.orphan", {"position": v(0, -37.5) * mm});
            skPoint(sketch, "E131.orphan", {"position": v(-75, 0) * mm});
            const initialGuessF40  = {"E128.0": [-0.075, -0.0375, 1, 0, 0.075, 0.0375, 1.1430642252800542, 1.9985284283097393]};
            skSetInitialGuess(sketch, initialGuessF40);
            skSolve(sketch);
        }
        {
            var Q0;
            {var subQ2=sQuery(id+"F40.wireOp",EDGE,"E128.0");Q0=makeQuery(id+"F40.imprint","IMPRINT",FACE,{"disambiguationData":[TD([[makeQuery(id+"F40.imprint","IMPRINT",EDGE,{"derivedFrom":subQ2}),1.0]])]});}
            extrude(context, id + "F41", {"entities" : qUnion([Q0]), "operationType" : NewBodyOperationType.REMOVE, "oppositeDirection" : true, "depth" : 152 * mm});
        }
        {
            var Q0;
            Q0=makeQuery(id+"F1.opExtrude","CAP_FACE",FACE,{"disambiguationData":[OSD([sQuery(id+"F0.wireOp",EDGE,"E3")])],"isStart":false});
            var sketch = newSketch(context, id + "F42", { "sketchPlane" : qUnion([Q0])});
            skLineSegment(sketch, "E132", {"start": v(-75, -37.5) * mm, "end": v(-75, -10.5) * mm});
            skLineSegment(sketch, "E133", {"start": v(-75, -10.5) * mm, "end": v(-65, -10.5) * mm});
            skLineSegment(sketch, "E134", {"start": v(-65, -10.5) * mm, "end": v(-65, -37.5) * mm});
            skLineSegment(sketch, "E135", {"start": v(-75, -10.5) * mm, "end": v(-85, -10.5) * mm});
            skLineSegment(sketch, "E136", {"start": v(-85, -10.5) * mm, "end": v(-85, -37.5) * mm});
            skLineSegment(sketch, "E137", {"start": v(-85, -37.5) * mm, "end": v(-65, -37.5) * mm});
            skLineSegment(sketch, "E138", {"start": v(-65, -10.5) * mm, "end": v(-65, -3.35) * mm});
            skLineSegment(sketch, "E139", {"start": v(-85, -10.5) * mm, "end": v(-85, -3.35) * mm});
            skLineSegment(sketch, "E140", {"start": v(-85, -3.35) * mm, "end": v(-65, -3.35) * mm});
            skCircle(sketch, "E141", {"center": v(-80, -6.94) * mm, "radius": 1.4 * mm});
            skCircle(sketch, "E142", {"center": v(-70, -6.94) * mm, "radius": 1.4 * mm});
            skLineSegment(sketch, "E143", {"start": v(-80, -6.94) * mm, "end": v(-70, -6.94) * mm, "construction": true});
            skLineSegment(sketch, "E144", {"start": v(-70, -3.38) * mm, "end": v(-70, -10.5) * mm});
            skSolve(sketch);
        }
        {
            var Q0;
            {var subQ0=sQuery(id+"F42.wireOp",EDGE,"E132");Q0=makeQuery(id+"F42.imprint","IMPRINT",FACE,{"disambiguationData":[TD([[makeQuery(id+"F42.imprint","IMPRINT",EDGE,{"derivedFrom":subQ0}),-1.0]])]});}
            var Q1;
            {var subQ0=sQuery(id+"F42.wireOp",EDGE,"E132");Q1=makeQuery(id+"F42.imprint","IMPRINT",FACE,{"disambiguationData":[TD([[makeQuery(id+"F42.imprint","IMPRINT",EDGE,{"derivedFrom":subQ0}),1.0]])]});}
            extrude(context, id + "F43", {"entities" : qUnion([Q0, Q1]), "operationType" : NewBodyOperationType.REMOVE, "oppositeDirection" : true, "depth" : 30 * mm});
        }
        {
            var Q0;
            Q0=makeQuery(id+"F42.imprint","IMPRINT",FACE,{"disambiguationData":[TD([[makeQuery(id+"F42.imprint","IMPRINT",EDGE,{"derivedFrom":sQuery(id+"F42.wireOp",EDGE,"E142")}),1.0]])]});
            var Q1;
            Q1=makeQuery(id+"F42.imprint","IMPRINT",FACE,{"disambiguationData":[TD([[makeQuery(id+"F42.imprint","IMPRINT",EDGE,{"derivedFrom":sQuery(id+"F42.wireOp",EDGE,"E141")}),1.0]])]});
            extrude(context, id + "F44", {"entities" : qUnion([Q0, Q1]), "operationType" : NewBodyOperationType.REMOVE, "oppositeDirection" : true, "depth" : 10 * mm});
        }
        {
            var Q0;
            Q0=makeQuery(id+"F41.boolean.opBoolean","COPY",FACE,{"derivedFrom":makeQuery(id+"F41.opExtrude","SWEPT_FACE",FACE,{"disambiguationData":[OSD([sQuery(id+"F40.wireOp",EDGE,"E127")])]})});
            var sketch = newSketch(context, id + "F45", { "sketchPlane" : qUnion([Q0])});
            skPoint(sketch, "E145", {"position": v(43.89, 62.5) * mm});
            skPoint(sketch, "E146", {"position": v(106.11, 62.5) * mm});
            skLineSegment(sketch, "E147", {"start": v(106.11, 62.5) * mm, "end": v(43.89, 62.5) * mm, "construction": true});
            skPoint(sketch, "E148", {"position": v(75, 62.5) * mm});
            skLineSegment(sketch, "E149.bottom", {"start": v(106.11, 93.61) * mm, "end": v(43.89, 93.61) * mm, "construction": true});
            skLineSegment(sketch, "E149.top", {"start": v(106.11, 31.39) * mm, "end": v(43.89, 31.39) * mm, "construction": true});
            skLineSegment(sketch, "E149.left", {"start": v(106.11, 93.61) * mm, "end": v(106.11, 31.39) * mm, "construction": true});
            skLineSegment(sketch, "E149.right", {"start": v(43.89, 93.61) * mm, "end": v(43.89, 31.39) * mm, "construction": true});
            skLineSegment(sketch, "E150", {"start": v(43.89, 82.2) * mm, "end": v(106.11, 82.2) * mm, "construction": true});
            skLineSegment(sketch, "E151", {"start": v(95.61, 33.52) * mm, "end": v(43.89, 33.52) * mm, "construction": true});
            skLineSegment(sketch, "E152", {"start": v(61.44, 75.4) * mm, "end": v(89.17, 75.4) * mm});
            skLineSegment(sketch, "E153", {"start": v(106.11, 62.5) * mm, "end": v(106.11, 33.52) * mm});
            skLineSegment(sketch, "E154", {"start": v(106.11, 48.01) * mm, "end": v(43.89, 48.01) * mm, "construction": true});
            skLineSegment(sketch, "E155", {"start": v(62.96, 62.5) * mm, "end": v(55.89, 48.01) * mm});
            skLineSegment(sketch, "E156", {"start": v(66.33, 69.4) * mm, "end": v(54.33, 69.4) * mm});
            skLineSegment(sketch, "E157", {"start": v(54.33, 69.4) * mm, "end": v(89.17, 69.4) * mm});
            skLineSegment(sketch, "E158", {"start": v(89.17, 75.4) * mm, "end": v(89.17, 69.4) * mm, "construction": true});
            skLineSegment(sketch, "E159", {"start": v(89.17, 62.5) * mm, "end": v(82.46, 62.5) * mm});
            skLineSegment(sketch, "E160", {"start": v(55.89, 82.2) * mm, "end": v(89.17, 82.2) * mm});
            skLineSegment(sketch, "E161", {"start": v(89.17, 82.2) * mm, "end": v(89.17, 62.5) * mm, "construction": true});
            skArc(sketch, "E162", {"start": v(89.17, 62.5) * mm, "mid": v(99.02, 72.35) * mm, "end": v(89.17, 82.2) * mm});
            skArc(sketch, "E163", {"start": v(89.17, 69.4) * mm, "mid": v(92.17, 72.4) * mm, "end": v(89.17, 75.4) * mm});
            skLineSegment(sketch, "E164.trimOffspring", {"start": v(82.46, 62.5) * mm, "end": v(103.33, 36.93) * mm});
            skLineSegment(sketch, "E165.trimOffspring", {"start": v(54.33, 69.4) * mm, "end": v(43.89, 48.01) * mm});
            skLineSegment(sketch, "E166.trimOffspring", {"start": v(71.96, 62.5) * mm, "end": v(92.83, 36.93) * mm});
            skLineSegment(sketch, "E167.trimOffspring", {"start": v(71.96, 62.5) * mm, "end": v(62.96, 62.5) * mm});
            skLineSegment(sketch, "E168", {"start": v(43.89, 48.01) * mm, "end": v(55.89, 48.01) * mm});
            skLineSegment(sketch, "E169", {"start": v(103.33, 36.93) * mm, "end": v(92.83, 36.93) * mm});
            skLineSegment(sketch, "E170", {"start": v(61.44, 75.4) * mm, "end": v(56.64, 75.4) * mm});
            skLineSegment(sketch, "E171", {"start": v(56.64, 75.4) * mm, "end": v(51.1, 82.2) * mm});
            skLineSegment(sketch, "E172", {"start": v(51.1, 82.2) * mm, "end": v(55.89, 82.2) * mm});
            skLineSegment(sketch, "E173", {"start": v(54.78, 80.45) * mm, "end": v(57.47, 77.15) * mm});
            skLineSegment(sketch, "E174", {"start": v(57.47, 77.15) * mm, "end": v(89.17, 77.15) * mm});
            skLineSegment(sketch, "E175", {"start": v(54.78, 80.45) * mm, "end": v(89.17, 80.45) * mm});
            skLineSegment(sketch, "E176", {"start": v(55.43, 67.65) * mm, "end": v(46.7, 49.76) * mm});
            skLineSegment(sketch, "E177", {"start": v(46.7, 49.76) * mm, "end": v(54.8, 49.76) * mm});
            skLineSegment(sketch, "E178", {"start": v(54.8, 49.76) * mm, "end": v(61.87, 64.25) * mm});
            skLineSegment(sketch, "E179", {"start": v(61.87, 64.25) * mm, "end": v(72.8, 64.25) * mm});
            skLineSegment(sketch, "E180", {"start": v(55.43, 67.65) * mm, "end": v(89.17, 67.65) * mm});
            skLineSegment(sketch, "E181", {"start": v(72.8, 64.25) * mm, "end": v(93.66, 38.68) * mm});
            skLineSegment(sketch, "E182", {"start": v(93.66, 38.68) * mm, "end": v(99.65, 38.68) * mm});
            skLineSegment(sketch, "E183", {"start": v(99.65, 38.68) * mm, "end": v(78.78, 64.25) * mm});
            skLineSegment(sketch, "E184.trimOffspring", {"start": v(78.78, 64.25) * mm, "end": v(89.17, 64.25) * mm});
            skArc(sketch, "E185", {"start": v(89.17, 67.65) * mm, "mid": v(93.92, 72.4) * mm, "end": v(89.17, 77.15) * mm});
            skArc(sketch, "E186", {"start": v(89.17, 64.25) * mm, "mid": v(97.27, 72.35) * mm, "end": v(89.17, 80.45) * mm});
            skSolve(sketch);
        }
        {
            var Q0;
            Q0=qSketchRegion(id+"F45",true);
            extrude(context, id + "F46", {"entities" : qUnion([Q0]), "operationType" : NewBodyOperationType.REMOVE, "oppositeDirection" : true, "depth" : 3 * mm});
        }
        {
            var Q0;
            Q0=makeQuery(id+"F1.opExtrude","CAP_FACE",FACE,{"disambiguationData":[OSD([sQuery(id+"F0.wireOp",EDGE,"E3")])],"isStart":true});
            var sketch = newSketch(context, id + "F47", { "sketchPlane" : qUnion([Q0])});
            skLineSegment(sketch, "E187.bottom", {"start": v(-19, 37.5) * mm, "end": v(-18.25, 37.5) * mm});
            skLineSegment(sketch, "E187.top", {"start": v(-19, 35) * mm, "end": v(-18.25, 35) * mm});
            skLineSegment(sketch, "E187.left", {"start": v(-19, 37.5) * mm, "end": v(-19, 35) * mm});
            skLineSegment(sketch, "E187.right", {"start": v(-18.25, 37.5) * mm, "end": v(-18.25, 35) * mm});
            skLineSegment(sketch, "E188.bottom", {"start": v(-131, 37.5) * mm, "end": v(-131.75, 37.5) * mm});
            skLineSegment(sketch, "E188.top", {"start": v(-131, 35) * mm, "end": v(-131.75, 35) * mm});
            skLineSegment(sketch, "E188.left", {"start": v(-131, 37.5) * mm, "end": v(-131, 35) * mm});
            skLineSegment(sketch, "E188.right", {"start": v(-131.75, 37.5) * mm, "end": v(-131.75, 35) * mm});
            skSolve(sketch);
        }
        {
            var Q0;
            Q0 = qSketchRegion(id + "F47", true);
            extrude(context, id + "F48", {"entities" : qUnion([Q0]), "operationType" : NewBodyOperationType.REMOVE, "oppositeDirection" : true, "depth" : 1.8 * mm});
        }
    });
